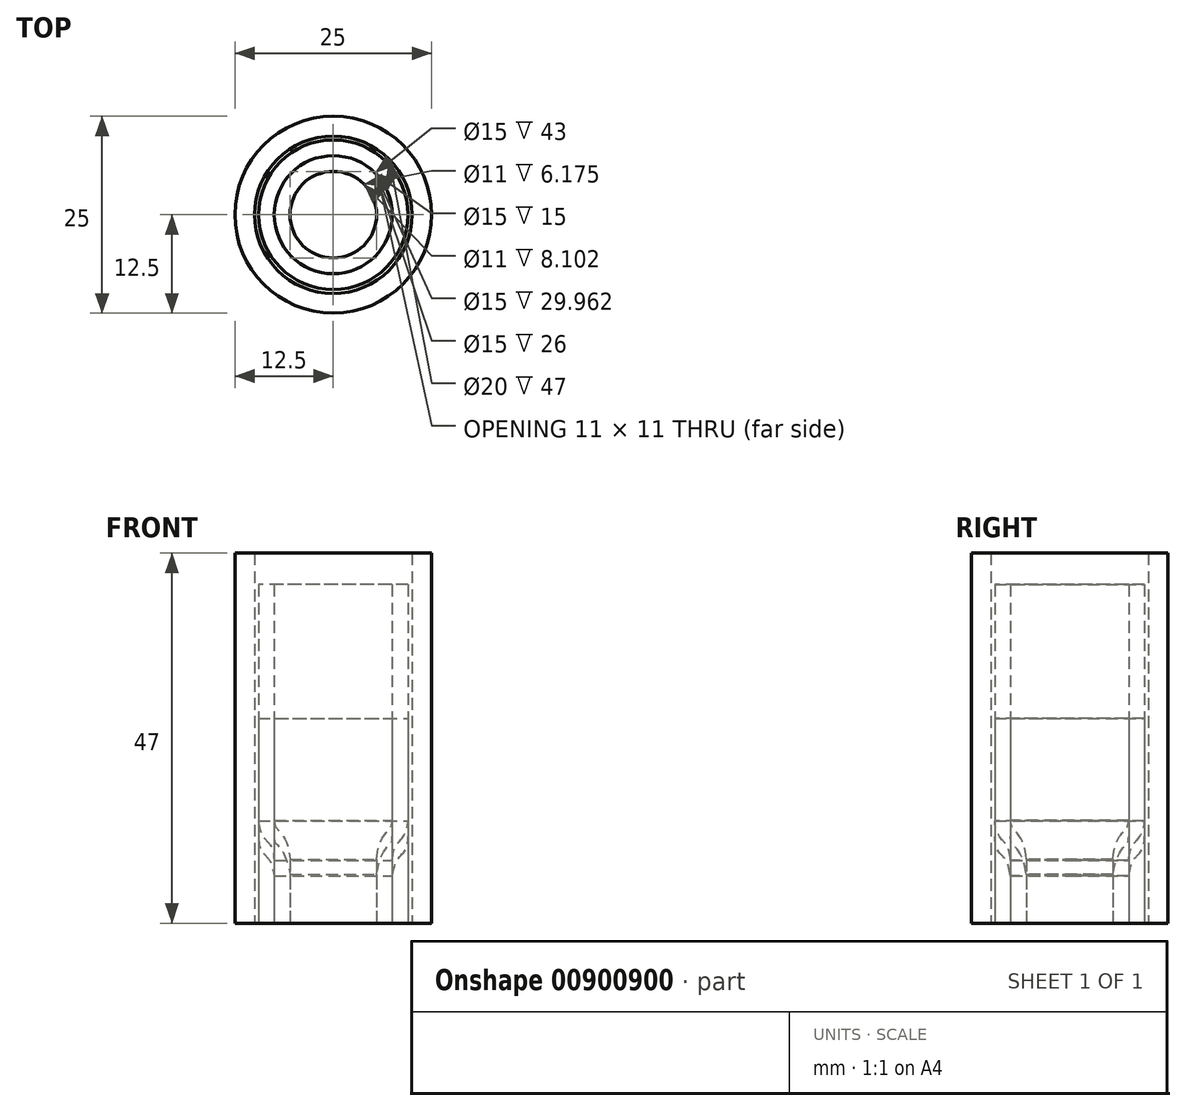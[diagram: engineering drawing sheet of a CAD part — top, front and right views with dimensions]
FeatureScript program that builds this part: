
annotation { "Feature Type Name" : "Feature", "Feature Type Description" : "" }
export const myFeature = defineFeature(function(context is Context, id is Id, definition is map)
    precondition{}
    {
        {
            var Q0;
            Q0=qCreatedBy(makeId("Top.planeOp"),FACE);
            var sketch = newSketch(context, id + "F0", { "sketchPlane" : qUnion([Q0])});
            skCircle(sketch, "E0", {"center": v(0, 0) * mm, "radius": 12.5 * mm});
            skCircle(sketch, "E1", {"center": v(0, 0) * mm, "radius": 10 * mm});
            skSolve(sketch);
        }
        {
            var Q0;
            Q0 = qSketchRegion(id + "F0", true);
            extrude(context, id + "F1", {"entities" : qUnion([Q0]), "depth" : 47 * mm, "offsetDistance" : 25 * mm});
        }
        {
            var Q0;
            Q0=qCreatedBy(makeId("Right.planeOp"),FACE);
            var sketch = newSketch(context, id + "F2", { "sketchPlane" : qUnion([Q0])});
            skLineSegment(sketch, "E2", {"start": v(-7.5, 0) * mm, "end": v(0, 0) * mm});
            skLineSegment(sketch, "E3", {"start": v(0, 0) * mm, "end": v(0, 26) * mm});
            skLineSegment(sketch, "E4", {"start": v(0, 26) * mm, "end": v(-9.5, 26) * mm});
            skLineSegment(sketch, "E5", {"start": v(-9.5, 26) * mm, "end": v(-9.5, 11) * mm});
            skLineSegment(sketch, "E6", {"start": v(-7.5, 0) * mm, "end": v(-7.5, 6) * mm});
            skFitSpline(sketch, "E7", {"points": [v(-9.5, 11) * mm, v(-8.5, 8.5) * mm, v(-7.5, 6) * mm], "startDerivative": vector(0.02, -9.9) * mm, "endDerivative": vector(1.65, -9.31) * mm});
            skSolve(sketch);
        }
        {
            var Q0;
            Q0 = qSketchRegion(id + "F2", true);
            var Q1;
            Q1=sQuery(id+"F2.wireOp",EDGE,"E3");
            revolve(context, id + "F3", {"surfaceOperationType" : NewSurfaceOperationType.NEW, "entities" : qUnion([Q0]), "axis" : qUnion([Q1]), "revolveType" : RevolveType.FULL});
        }
        {
            var Q0;
            Q0=makeQuery(id+"F3.opRevolve","SWEPT_FACE",FACE,{"disambiguationData":[OSD([sQuery(id+"F2.wireOp",EDGE,"E4")])]});
            var Q1;
            Q1=makeQuery(id+"F3.opRevolve","SWEPT_FACE",FACE,{"disambiguationData":[OSD([sQuery(id+"F2.wireOp",EDGE,"E2")])]});
            shell(context, id + "F4", {"entities" : qUnion([Q0, Q1]), "thickness" : 2 * mm});
        }
        {
            var Q0;
            Q0=qCreatedBy(makeId("Right.planeOp"),FACE);
            var sketch = newSketch(context, id + "F5", { "sketchPlane" : qUnion([Q0])});
            skLineSegment(sketch, "E8", {"start": v(262.85, 178.96) * mm, "end": v(270.35, 178.96) * mm});
            skLineSegment(sketch, "E9", {"start": v(270.35, 178.96) * mm, "end": v(270.35, 204.96) * mm});
            skLineSegment(sketch, "E10", {"start": v(270.35, 204.96) * mm, "end": v(260.85, 204.96) * mm});
            skLineSegment(sketch, "E11", {"start": v(260.85, 204.96) * mm, "end": v(260.85, 192.96) * mm});
            skLineSegment(sketch, "E12", {"start": v(262.85, 178.96) * mm, "end": v(262.85, 184.96) * mm});
            skFitSpline(sketch, "E13", {"points": [v(260.85, 192.96) * mm, v(261.85, 188.96) * mm, v(262.85, 184.96) * mm], "startDerivative": vector(1.07, -18.42) * mm, "endDerivative": vector(-1.18, -9.82) * mm});
            skLineSegment(sketch, "E14", {"start": v(-7.5, 0) * mm, "end": v(0, 0) * mm});
            skLineSegment(sketch, "E15", {"start": v(0, 0) * mm, "end": v(0, 43) * mm});
            skLineSegment(sketch, "E16", {"start": v(0, 43) * mm, "end": v(-9.5, 43) * mm});
            skLineSegment(sketch, "E17", {"start": v(-9.5, 43) * mm, "end": v(-9.5, 13) * mm});
            skLineSegment(sketch, "E18", {"start": v(-7.5, 0) * mm, "end": v(-7.5, 8) * mm});
            skFitSpline(sketch, "E19", {"points": [v(-9.5, 13) * mm, v(-8.5, 10.5) * mm, v(-7.5, 8) * mm], "startDerivative": vector(0.25, -7.4) * mm, "endDerivative": vector(1.07, -10.5) * mm});
            skSolve(sketch);
        }
        {
            var Q0;
            Q0 = qSketchRegion(id + "F5", true);
            var Q1;
            Q1=sQuery(id+"F5.wireOp",EDGE,"E15");
            revolve(context, id + "F6", {"surfaceOperationType" : NewSurfaceOperationType.NEW, "entities" : qUnion([Q0]), "axis" : qUnion([Q1]), "revolveType" : RevolveType.FULL});
        }
        {
            var Q0;
            Q0=makeQuery(id+"F6.opRevolve","SWEPT_FACE",FACE,{"disambiguationData":[OSD([sQuery(id+"F5.wireOp",EDGE,"E16")])]});
            var Q1;
            Q1=makeQuery(id+"F6.opRevolve","SWEPT_FACE",FACE,{"disambiguationData":[OSD([sQuery(id+"F5.wireOp",EDGE,"E14")])]});
            shell(context, id + "F7", {"entities" : qUnion([Q0, Q1]), "thickness" : 2 * mm});
        }
        {
            var Q0;
            Q0=makeQuery(id+"F6.opRevolve","SWEPT_BODY",BODY,{"disambiguationData":[OSD([sQuery(id+"F5.wireOp",EDGE,"E8"),sQuery(id+"F5.wireOp",EDGE,"E9"),sQuery(id+"F5.wireOp",EDGE,"E10"),sQuery(id+"F5.wireOp",EDGE,"E11"),sQuery(id+"F5.wireOp",EDGE,"E12"),sQuery(id+"F5.wireOp",EDGE,"E13")])]});
            deleteBodies(context, id + "F8", {"entities" : qUnion([Q0])});
        }
        {
            var Q0;
            Q0=qCreatedBy(makeId("Top.planeOp"),FACE);
            var sketch = newSketch(context, id + "F9", { "sketchPlane" : qUnion([Q0])});
            skCircle(sketch, "E20", {"center": v(0, 0) * mm, "radius": 9.5 * mm});
            skCircle(sketch, "E21", {"center": v(0, 0) * mm, "radius": 7.5 * mm});
            skSolve(sketch);
        }
        {
            var Q0;
            Q0 = qSketchRegion(id + "F9", true);
            extrude(context, id + "F10", {"entities" : qUnion([Q0]), "depth" : 26 * mm, "offsetDistance" : 25 * mm});
        }
        {
            var Q0;
            Q0 = qSketchRegion(id + "F9", true);
            extrude(context, id + "F11", {"entities" : qUnion([Q0]), "depth" : 43 * mm, "offsetDistance" : 25 * mm});
        }
    });
